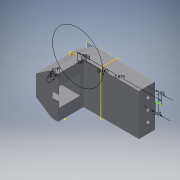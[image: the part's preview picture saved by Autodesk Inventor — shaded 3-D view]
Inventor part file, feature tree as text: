
AUTODESK INVENTOR PART (.ipt)
format: ipt  version: 2016 (Build 200138000, 138)  size: 532,480 bytes
history: native  units: in
note: dims shown in document units (in); Inventor stores cm internally (conversion verified against a paired STEP export)
features: sketch x23, extrude x19, projected_geometry x13, plane x6, reference x6, fillet x1
ambient origin geometry x8: Origin, YZ Plane, XZ Plane, XY Plane, X Axis, Y Axis, Z Axis, Center Point
bodies: Solid1 (feature_tree)
feature tree (68):
  plane  "Work Plane1"
  plane  "Work Plane2"
  sketch  "Sketch1"  dims[d0=0.1in d1=0.1in]
  plane  "Work Plane3"
  sketch  "Sketch2"  dims[d2=0.15in d3=0.35in]
  plane  "Work Plane4"
  sketch  "Sketch3"  dims[d4=0.35in d5=7.874in d6=0.0in]
  extrude  "Extrusion1"  Depth=0.1in
  extrude  "Extrusion2"  Depth=0.35in
  extrude  "Extrusion3"  Depth=0.35in
  fillet  "Fillet1"  [1 undecoded]
  extrude  "Extrusion4"  Depth=0.35in
  extrude  "Extrusion5"  TaperAngle=180.0deg  [1 undecoded]
  extrude  "Extrusion6"  Depth=0.35in
  extrude  "Extrusion7"  Depth=1.25in TaperAngle=0.0deg
  extrude  "Extrusion8"  Depth=0.15in TaperAngle=0.0deg
  extrude  "Extrusion9"  Depth=0.146in
  extrude  "Extrusion10"  Depth=170.0in TaperAngle=0.0deg
  extrude  "Extrusion11"  Depth=170.0in TaperAngle=0.0deg
  extrude  "Extrusion12"  Depth=0.2953in TaperAngle=0.0deg
  sketch  "Sketch15"  dims[d39=0.25in d40=0.0in d41=2.225in]
  sketch  "Sketch16"  dims[d42=1.9in d43=1.9in]
  extrude  "Extrusion13"  Depth=0.35in TaperAngle=0.0deg
  extrude  "Extrusion14"  Depth=0.0547in TaperAngle=0.0deg
  extrude  "Extrusion15"  Depth=0.25in
  extrude  "Extrusion16"  Depth=1.9in
  sketch  "Sketch20"  dims[d62=0.1in d63=0.0in]
  extrude  "Extrusion17"  Depth=1.378in
  extrude  "Extrusion18"  Depth=0.6102in
  plane  "Work Plane5"
  extrude  "Extrusion19"  Depth=0.1in TaperAngle=0.0deg
  plane  "Work Plane6"
  reference  "Reference1"
  reference  "Reference2"
  sketch  "Sketch4"  dims[d8=0.25in d9=0.35in]
  projected_geometry  "Projected Loop1"
  sketch  "Sketch5"  dims[d10=4.61in d11=180.0deg]
  projected_geometry  "Projected Loop2"
  sketch  "Sketch6"  dims[d12=4.61in d13=0.35in]
  reference  "Reference3"
  reference  "Reference4"
  sketch  "Sketch7"  dims[d14=1.25in d15=0.0in d16=1.25in d17=0.0in]
  reference  "Reference5"
  sketch  "Sketch8"  dims[d18=0.15in d19=1.25in d20=0.0in]
  projected_geometry  "Projected Loop3"
  sketch  "Sketch9"  dims[d21=0.146in d22=0.315in]
  projected_geometry  "Projected Loop4"
  sketch  "Sketch10"  dims[d23=0.315in d24=170.0in d25=0.0in]
  projected_geometry  "Projected Loop5"
  sketch  "Sketch11"  dims[d26=0.315in d27=170.0in d28=0.0in]
  projected_geometry  "Projected Loop6"
  sketch  "Sketch12"  dims[d29=0.8661in d30=0.2953in d31=0.0in]
  projected_geometry  "Projected Loop7"
  sketch  "Sketch13"  dims[d32=0.35in d33=0.0in d34=0.3in d35=0.0in]
  sketch  "Sketch14"  dims[d36=0.315in d37=0.0547in d38=0.0in]
  projected_geometry  "Projected Loop8"
  projected_geometry  "Projected Loop9"
  sketch  "Sketch17"  dims[d44=0.689in d45=1.378in]
  projected_geometry  "Projected Loop10"
  sketch  "Sketch18"  dims[d47=0.6102in d51=0.1181in]
  projected_geometry  "Projected Loop11"
  sketch  "Sketch19"  dims[d52=0.7874in d54=1.2205in d55=0.7874in d57=1.2205in d60=0.1in d61=0.0in]
  reference  "Reference6"
  sketch  "Sketch21"  dims[d64=1.9685in]
  projected_geometry  "Projected Loop12"
  sketch  "Sketch22"  dims[d65=0.0in]
  projected_geometry  "Projected Loop13"
  sketch  "Sketch23"  dims[d66=0.8268in d67=0.0in d68=0.325in d69=0.0in d70=1.9685in d71=0.0in d72=0.325in d73=0.0in d74=1.7717in d75=0.325in d76=0.0in d77=1.7323in d78=1.975in d79=0.0in d80=0.1in d81=0.0in d82=1.1811in d83=0.5118in d84=0.2875in d85=0.0in d86=-3.5in d87=0.8661in d88=0.2953in d89=0.0in d90=-3.5in]
note: 2 required parameter values undecoded (feature->parameter linkage not recoverable at this tier; creation-order binding heuristic only, values carry confidence <= 0.55)
